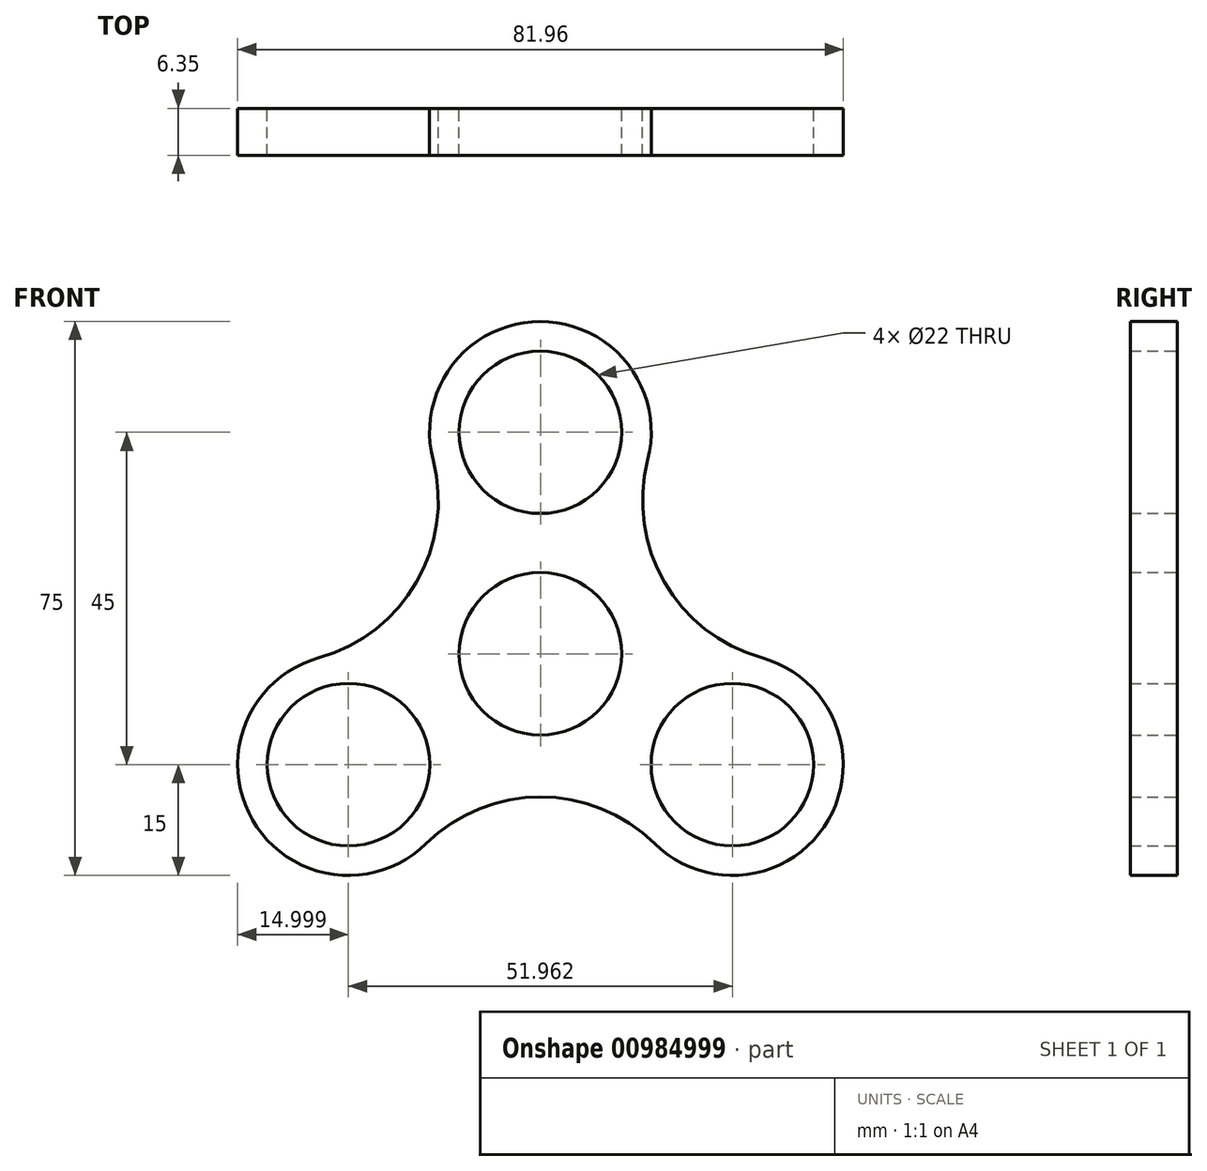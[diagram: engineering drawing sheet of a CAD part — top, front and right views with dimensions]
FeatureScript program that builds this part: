
annotation { "Feature Type Name" : "Feature", "Feature Type Description" : "" }
export const myFeature = defineFeature(function(context is Context, id is Id, definition is map)
    precondition{}
    {
        {
            var Q0;
            Q0=qCreatedBy(makeId("Front.planeOp"),FACE);
            var sketch = newSketch(context, id + "F0", { "sketchPlane" : qUnion([Q0])});
            skCircle(sketch, "E0.cCircle", {"center": v(0, 0) * mm, "radius": 30 * mm, "construction": true});
            skLineSegment(sketch, "E0.0", {"start": v(51.96, -30) * mm, "end": v(-51.96, -30) * mm, "construction": true});
            skLineSegment(sketch, "E0.1", {"start": v(-51.96, -30) * mm, "end": v(0, 60) * mm, "construction": true});
            skLineSegment(sketch, "E0.2", {"start": v(0, 60) * mm, "end": v(51.96, -30) * mm, "construction": true});
            skPoint(sketch, "E0.0.midPoint", {"position": v(0, -30) * mm});
            skArc(sketch, "E1", {"start": v(14.52, 26.25) * mm, "mid": v(0, 45) * mm, "end": v(-14.52, 26.25) * mm});
            skArc(sketch, "E2", {"start": v(15.47, -25.7) * mm, "mid": v(38.97, -22.5) * mm, "end": v(30, -0.55) * mm});
            skArc(sketch, "E3", {"start": v(-30, -0.55) * mm, "mid": v(-38.97, -22.5) * mm, "end": v(-15.47, -25.7) * mm});
            skCircle(sketch, "E4", {"center": v(0, 30) * mm, "radius": 11 * mm});
            skCircle(sketch, "E5", {"center": v(0, 0) * mm, "radius": 11 * mm});
            skCircle(sketch, "E6", {"center": v(25.98, -15) * mm, "radius": 11 * mm});
            skCircle(sketch, "E7", {"center": v(-25.98, -15) * mm, "radius": 11 * mm});
            skArc(sketch, "E8.2.0", {"start": v(14.52, 26.25) * mm, "mid": v(16.78, 9.69) * mm, "end": v(30, -0.55) * mm});
            skArc(sketch, "E9.1.0", {"start": v(-30, -0.55) * mm, "mid": v(-16.78, 9.69) * mm, "end": v(-14.52, 26.25) * mm});
            skArc(sketch, "E9.2.0", {"start": v(15.47, -25.7) * mm, "mid": v(0, -19.38) * mm, "end": v(-15.47, -25.7) * mm});
            skSolve(sketch);
        }
        {
            var Q0;
            Q0 = qSketchRegion(id + "F0", true);
            extrude(context, id + "F1", {"entities" : qUnion([Q0]), "depth" : 6.35 * mm, "offsetDistance" : 25.4 * mm});
        }
    });
